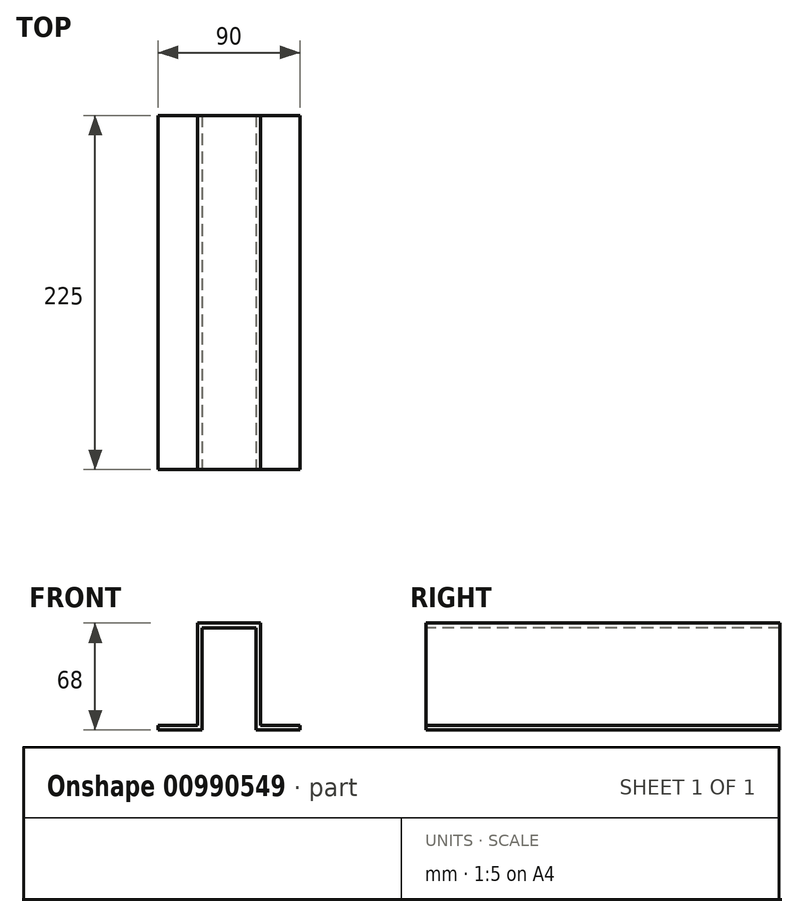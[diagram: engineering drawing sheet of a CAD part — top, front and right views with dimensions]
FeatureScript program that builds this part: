
annotation { "Feature Type Name" : "Feature", "Feature Type Description" : "" }
export const myFeature = defineFeature(function(context is Context, id is Id, definition is map)
    precondition{}
    {
        {
            var Q0;
            Q0=qCreatedBy(makeId("Front.planeOp"),FACE);
            var sketch = newSketch(context, id + "F0", { "sketchPlane" : qUnion([Q0])});
            skLineSegment(sketch, "E0", {"start": v(-45, -20) * mm, "end": v(-20, -20) * mm});
            skLineSegment(sketch, "E1", {"start": v(-20, -20) * mm, "end": v(-20, 45) * mm});
            skLineSegment(sketch, "E2", {"start": v(-20, 45) * mm, "end": v(20, 45) * mm});
            skLineSegment(sketch, "E3", {"start": v(20, 45) * mm, "end": v(20, -20) * mm});
            skLineSegment(sketch, "E4", {"start": v(20, -20) * mm, "end": v(45, -20) * mm});
            skLineSegment(sketch, "E5", {"start": v(-45, -20) * mm, "end": v(-45, -23) * mm});
            skLineSegment(sketch, "E6", {"start": v(-45, -23) * mm, "end": v(-17, -23) * mm});
            skLineSegment(sketch, "E7", {"start": v(-17, -23) * mm, "end": v(-17, 42) * mm});
            skLineSegment(sketch, "E8", {"start": v(-17, 42) * mm, "end": v(17, 42) * mm});
            skLineSegment(sketch, "E9", {"start": v(17, 42) * mm, "end": v(17, -23) * mm});
            skLineSegment(sketch, "E10", {"start": v(17, -23) * mm, "end": v(45, -23) * mm});
            skLineSegment(sketch, "E11", {"start": v(45, -23) * mm, "end": v(45, -20) * mm});
            skSolve(sketch);
        }
        {
            var Q0;
            Q0=makeQuery(id+"F0.imprint","IMPRINT",FACE,{"disambiguationData":[TD([[makeQuery(id+"F0.imprint","IMPRINT",EDGE,{"derivedFrom":sQuery(id+"F0.wireOp",EDGE,"E0")}),-1.0]])]});
            extrude(context, id + "F1", {"entities" : qUnion([Q0]), "oppositeDirection" : true, "depth" : 225 * mm, "offsetDistance" : 25 * mm});
        }
    });
